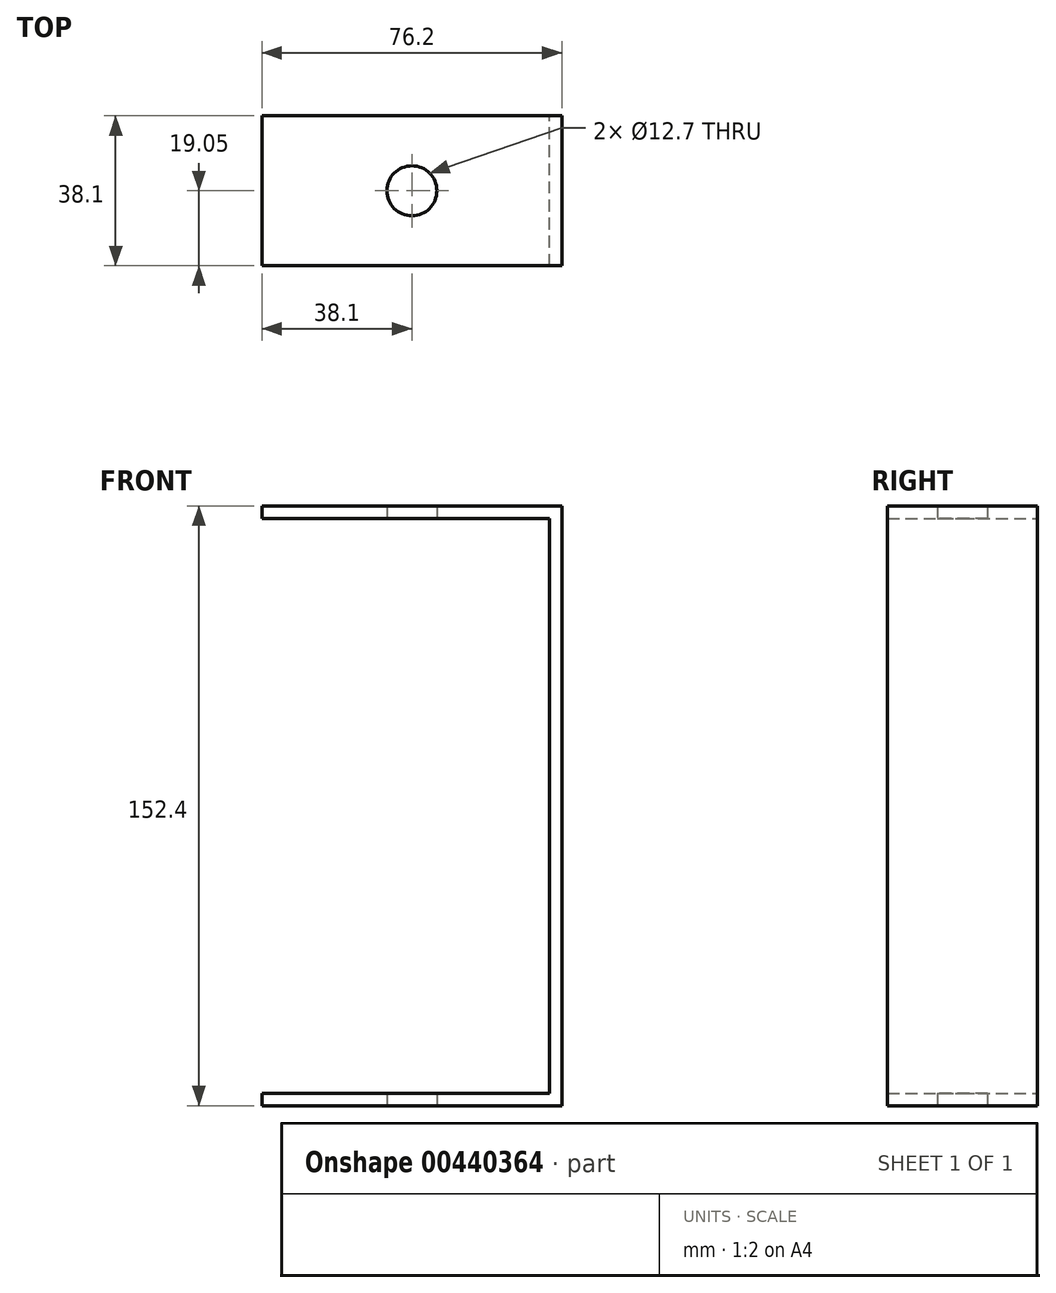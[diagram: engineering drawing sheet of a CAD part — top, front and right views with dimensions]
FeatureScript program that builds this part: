
annotation { "Feature Type Name" : "Feature", "Feature Type Description" : "" }
export const myFeature = defineFeature(function(context is Context, id is Id, definition is map)
    precondition{}
    {
        {
            var Q0;
            Q0=qCreatedBy(makeId("Front.planeOp"),FACE);
            var sketch = newSketch(context, id + "F0", { "sketchPlane" : qUnion([Q0])});
            skLineSegment(sketch, "E0.bottom", {"start": v(-38.1, 76.2) * mm, "end": v(38.1, 76.2) * mm});
            skLineSegment(sketch, "E0.top", {"start": v(-38.1, -76.2) * mm, "end": v(38.1, -76.2) * mm});
            skLineSegment(sketch, "E0.left", {"start": v(-38.1, 76.2) * mm, "end": v(-38.1, -76.2) * mm});
            skLineSegment(sketch, "E0.right", {"start": v(38.1, 76.2) * mm, "end": v(38.1, -76.2) * mm});
            skPoint(sketch, "E0.middle", {"position": v(0, 0) * mm});
            skLineSegment(sketch, "E1.bottom", {"start": v(-38.1, 73.03) * mm, "end": v(34.93, 73.03) * mm});
            skLineSegment(sketch, "E1.top", {"start": v(-38.1, -73.02) * mm, "end": v(34.93, -73.02) * mm});
            skLineSegment(sketch, "E1.left", {"start": v(-38.1, 73.03) * mm, "end": v(-38.1, -73.02) * mm});
            skLineSegment(sketch, "E1.right", {"start": v(34.93, 73.03) * mm, "end": v(34.93, -73.03) * mm});
            skSolve(sketch);
        }
        {
            var Q0;
            {var subQ4=sQuery(id+"F0.wireOp",EDGE,"E0.bottom");Q0=makeQuery(id+"F0.imprint","IMPRINT",FACE,{"disambiguationData":[TD([[makeQuery(id+"F0.imprint","IMPRINT",EDGE,{"derivedFrom":subQ4}),-1.0]])]});}
            extrude(context, id + "F1", {"entities" : qUnion([Q0]), "endBound" : BoundingType.SYMMETRIC, "depth" : 38.1 * mm});
        }
        {
            var Q0;
            Q0=makeQuery(id+"F1.opExtrude","SWEPT_FACE",FACE,{"disambiguationData":[OSD([sQuery(id+"F0.wireOp",EDGE,"E0.top")])]});
            var sketch = newSketch(context, id + "F2", { "sketchPlane" : qUnion([Q0])});
            skCircle(sketch, "E2", {"center": v(0, 0) * mm, "radius": 6.35 * mm});
            skSolve(sketch);
        }
        {
            var Q0;
            Q0=makeQuery(id+"F2.imprint","IMPRINT",FACE,{"disambiguationData":[TD([[makeQuery(id+"F2.imprint","IMPRINT",EDGE,{"derivedFrom":sQuery(id+"F2.wireOp",EDGE,"E2")}),1.0]])]});
            extrude(context, id + "F3", {"entities" : qUnion([Q0]), "operationType" : NewBodyOperationType.REMOVE, "endBound" : BoundingType.SYMMETRIC, "oppositeDirection" : true, "depth" : 6.35 * mm});
        }
        {
            var Q0;
            Q0=makeQuery(id+"F1.opExtrude","SWEPT_FACE",FACE,{"disambiguationData":[OSD([sQuery(id+"F0.wireOp",EDGE,"E0.bottom")])]});
            var sketch = newSketch(context, id + "F4", { "sketchPlane" : qUnion([Q0])});
            skCircle(sketch, "E3", {"center": v(0, 0) * mm, "radius": 6.35 * mm});
            skSolve(sketch);
        }
        {
            var Q0;
            Q0=makeQuery(id+"F4.imprint","IMPRINT",FACE,{"disambiguationData":[TD([[makeQuery(id+"F4.imprint","IMPRINT",EDGE,{"derivedFrom":sQuery(id+"F4.wireOp",EDGE,"E3")}),1.0]])]});
            extrude(context, id + "F5", {"entities" : qUnion([Q0]), "operationType" : NewBodyOperationType.REMOVE, "endBound" : BoundingType.SYMMETRIC, "depth" : 6.35 * mm});
        }
    });
